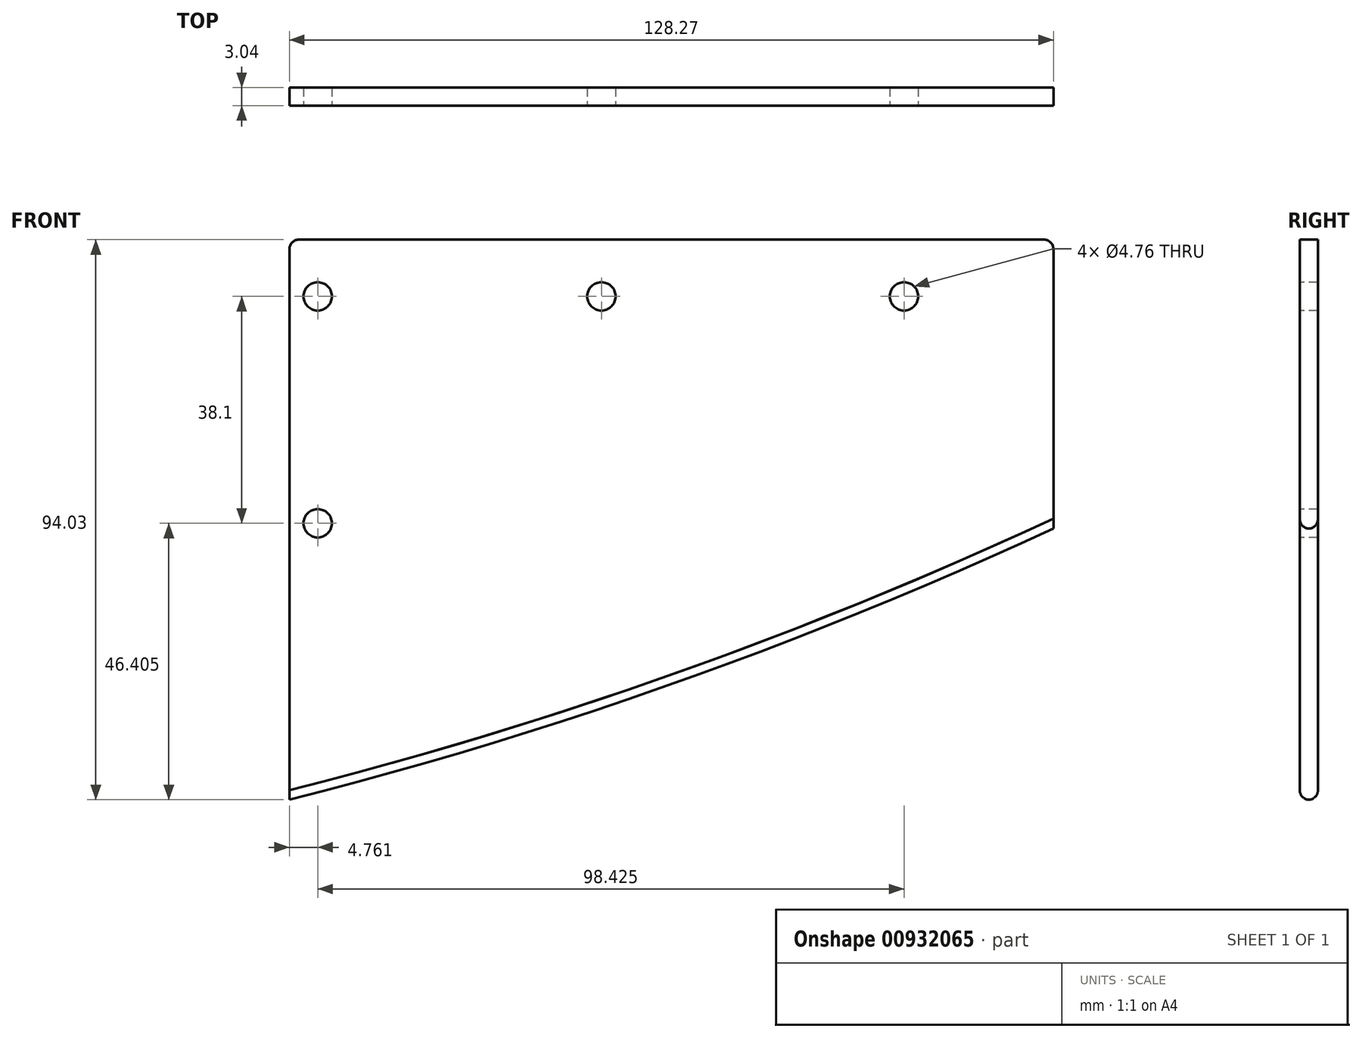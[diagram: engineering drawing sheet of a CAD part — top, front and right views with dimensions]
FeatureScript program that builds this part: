
annotation { "Feature Type Name" : "Feature", "Feature Type Description" : "" }
export const myFeature = defineFeature(function(context is Context, id is Id, definition is map)
    precondition{}
    {
        {
            var Q0;
            Q0=qCreatedBy(makeId("Front.planeOp"),FACE);
            var sketch = newSketch(context, id + "F0", { "sketchPlane" : qUnion([Q0])});
            skLineSegment(sketch, "E0", {"start": v(0, 50.8) * mm, "end": v(0, -50.8) * mm, "construction": true});
            skLineSegment(sketch, "E1", {"start": v(-76.2, -27.05) * mm, "end": v(68.52, 24.32) * mm, "construction": true});
            skFitSpline(sketch, "E2", {"points": [v(-65.2, -19.76) * mm, v(-51.97, -16.28) * mm, v(-38.84, -12.57) * mm, v(-25.8, -8.61) * mm, v(-12.85, -4.42) * mm, v(0, 0) * mm, v(12.78, 4.67) * mm, v(25.45, 9.58) * mm, v(38.07, 14.73) * mm, v(50.6, 20.12) * mm, v(63.07, 25.76) * mm], "startDerivative": vector(217.9, 45.9) * mm, "endDerivative": vector(67.85, 134.75) * mm, "construction": true});
            skFitSpline(sketch, "E3", {"points": [v(-65.2, -19.76) * mm, v(-51.97, -16.28) * mm, v(-38.84, -12.57) * mm, v(-25.8, -8.61) * mm, v(-12.85, -4.42) * mm, v(0, 0) * mm, v(12.78, 4.67) * mm, v(25.45, 9.58) * mm, v(38.07, 14.73) * mm, v(50.6, 20.12) * mm, v(63.07, 25.76) * mm], "startDerivative": vector(132.25, 34.26) * mm, "endDerivative": vector(124.31, 56.8) * mm});
            skLineSegment(sketch, "E4", {"start": v(-65.2, -19.76) * mm, "end": v(-65.2, 74.27) * mm});
            skLineSegment(sketch, "E5", {"start": v(63.07, 25.76) * mm, "end": v(63.07, 74.27) * mm});
            skLineSegment(sketch, "E6", {"start": v(-65.2, 74.27) * mm, "end": v(63.07, 74.27) * mm});
            skSolve(sketch);
        }
        {
            var Q0;
            Q0 = qSketchRegion(id + "F0", true);
            extrude(context, id + "F1", {"entities" : qUnion([Q0]), "depth" : 3.04 * mm, "offsetDistance" : 25.4 * mm});
        }
        {
            var Q0;
            Q0=makeQuery(id+"F1.opExtrude","CAP_FACE",FACE,{"disambiguationData":[OSD([sQuery(id+"F0.wireOp",EDGE,"E3"),sQuery(id+"F0.wireOp",EDGE,"E4"),sQuery(id+"F0.wireOp",EDGE,"byqLgHS4-dwKe-VCBX-0srA-KfMLztwxdTMz")])],"isStart":false});
            var sketch = newSketch(context, id + "F2", { "sketchPlane" : qUnion([Q0])});
            skCircle(sketch, "E7", {"center": v(-60.44, 64.74) * mm, "radius": 2.38 * mm});
            skCircle(sketch, "E8", {"center": v(-60.44, 26.64) * mm, "radius": 2.38 * mm});
            skCircle(sketch, "E9", {"center": v(-12.81, 64.74) * mm, "radius": 2.38 * mm});
            skCircle(sketch, "E10", {"center": v(37.99, 64.74) * mm, "radius": 2.38 * mm});
            skSolve(sketch);
        }
        {
            var Q0;
            Q0 = qSketchRegion(id + "F2", true);
            var Q1;
            Q1=makeQuery(id+"F1.opExtrude","CAP_FACE",FACE,{"disambiguationData":[OSD([sQuery(id+"F0.wireOp",EDGE,"E3"),sQuery(id+"F0.wireOp",EDGE,"E4"),sQuery(id+"F0.wireOp",EDGE,"byqLgHS4-dwKe-VCBX-0srA-KfMLztwxdTMz")])],"isStart":true});
            extrude(context, id + "F3", {"entities" : qUnion([Q0]), "operationType" : NewBodyOperationType.REMOVE, "endBound" : BoundingType.UP_TO_SURFACE, "oppositeDirection" : true, "depth" : 25.4 * mm, "endBoundEntityFace" : qUnion([Q1]), "offsetDistance" : 25.4 * mm});
        }
        {
            var Q0;
            Q0=makeQuery(id+"F1.opExtrude","SWEPT_EDGE",EDGE,{"disambiguationData":[OSD([sQuery(id+"F0.wireOp",EDGE,"E4"),sQuery(id+"F0.wireOp",EDGE,"E6")])]});
            var Q1;
            Q1=makeQuery(id+"F1.opExtrude","SWEPT_EDGE",EDGE,{"disambiguationData":[OSD([sQuery(id+"F0.wireOp",EDGE,"E5"),sQuery(id+"F0.wireOp",EDGE,"E6")])]});
            fillet(context, id + "F4", {"entities" : qUnion([Q0, Q1]), "radius" : 1.59 * mm, "tangentPropagation" : true, "allowEdgeOverflow" : false});
        }
        {
            var Q0;
            Q0=makeQuery(id+"F1.opExtrude","CAP_EDGE",EDGE,{"disambiguationData":[OSD([sQuery(id+"F0.wireOp",EDGE,"E3")])],"isStart":false});
            var Q1;
            Q1=makeQuery(id+"F1.opExtrude","CAP_EDGE",EDGE,{"disambiguationData":[OSD([sQuery(id+"F0.wireOp",EDGE,"E3")])],"isStart":true});
            fillet(context, id + "F5", {"entities" : qUnion([Q0, Q1]), "radius" : 1.52 * mm, "tangentPropagation" : true, "allowEdgeOverflow" : false});
        }
    });
